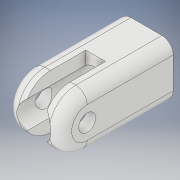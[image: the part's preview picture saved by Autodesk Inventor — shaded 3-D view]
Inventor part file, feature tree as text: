
AUTODESK INVENTOR PART (.ipt)
format: ipt  version: 2017 SP1 (Build 210196100, 196)  size: 192,000 bytes
history: native  units: in
note: dims shown in document units (in); Inventor stores cm internally (conversion verified against a paired STEP export)
features: extrude x5, sketch x5, fillet x1, projected_geometry x1
ambient origin geometry x8: Origin, YZ Plane, XZ Plane, XY Plane, X Axis, Y Axis, Z Axis, Center Point
bodies: Solid1 (feature_tree)
feature tree (12):
  extrude  "Extrusion1"  Depth=0.374in
  extrude  "Extrusion2"  Depth=0.374in
  extrude  "Extrusion3"  Depth=0.1181in
  fillet  "Fillet1"  Radius=0.1181in
  extrude  "Extrusion4"  Depth=0.0787in
  extrude  "Extrusion5"  Depth=0.1181in TaperAngle=0.0deg
  sketch  "Sketch1"  dims[d0=0.374in d1=0.374in]
  sketch  "Sketch2"  dims[d2=0.3543in d3=0.0in d4=0.374in]
  sketch  "Sketch3"  dims[d5=0.6004in d6=0.1181in d7=0.1181in d8=0.0in]
  projected_geometry  "Projected Loop1"
  sketch  "Sketch4"  dims[d9=0.1181in d10=0.0in d11=0.0787in]
  sketch  "Sketch5"  dims[d12=0.1181in d13=0.1181in d14=0.0in d15=0.2362in d16=0.5906in d17=0.0in d18=0.2362in d19=0.0in]
